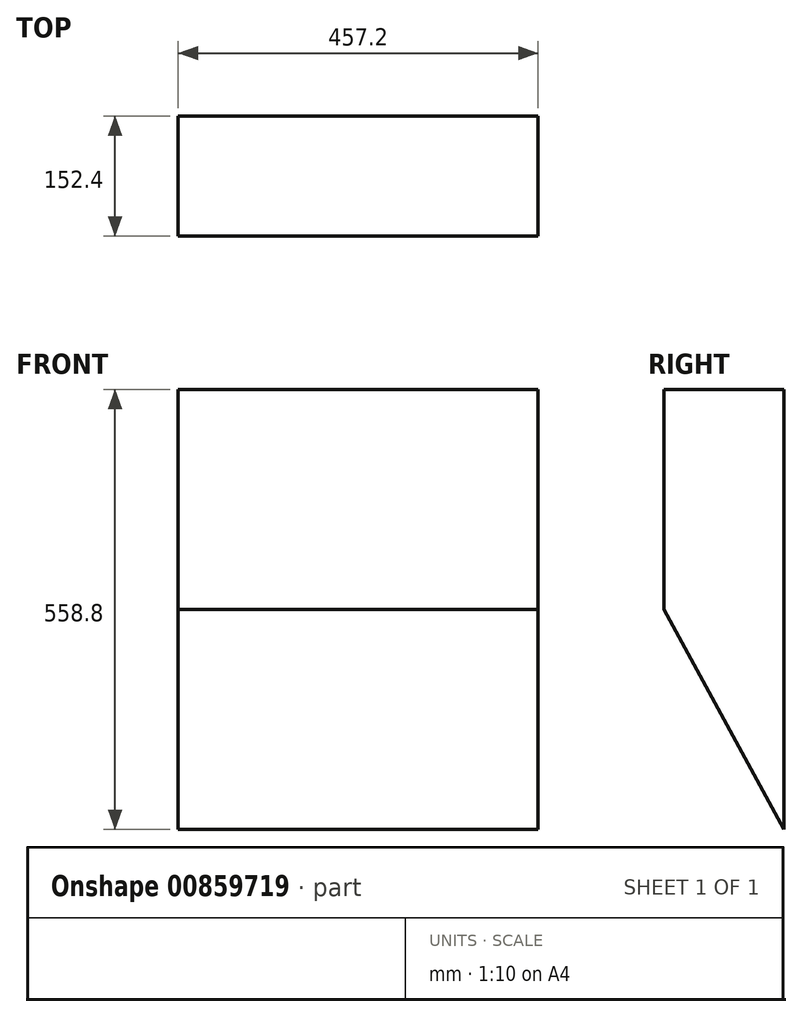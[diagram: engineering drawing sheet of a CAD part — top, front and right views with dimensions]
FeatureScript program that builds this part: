
annotation { "Feature Type Name" : "Feature", "Feature Type Description" : "" }
export const myFeature = defineFeature(function(context is Context, id is Id, definition is map)
    precondition{}
    {
        {
            var Q0;
            Q0=qCreatedBy(makeId("Right.planeOp"),FACE);
            var sketch = newSketch(context, id + "F0", { "sketchPlane" : qUnion([Q0])});
            skLineSegment(sketch, "E0.bottom", {"start": v(31.31, 467.97) * mm, "end": v(-121.09, 467.97) * mm, "construction": true});
            skLineSegment(sketch, "E0.top", {"start": v(31.31, -90.83) * mm, "end": v(-121.09, -90.83) * mm, "construction": true});
            skLineSegment(sketch, "E0.left", {"start": v(31.31, 467.97) * mm, "end": v(31.31, -90.83) * mm, "construction": true});
            skLineSegment(sketch, "E0.right", {"start": v(-121.09, 467.97) * mm, "end": v(-121.09, -90.83) * mm, "construction": true});
            skLineSegment(sketch, "E1", {"start": v(31.31, 467.97) * mm, "end": v(-121.09, 467.97) * mm});
            skLineSegment(sketch, "E2", {"start": v(-121.09, 188.57) * mm, "end": v(31.31, -90.83) * mm});
            skLineSegment(sketch, "E3", {"start": v(31.31, 467.97) * mm, "end": v(31.31, -90.83) * mm});
            skLineSegment(sketch, "E4", {"start": v(-121.09, 188.57) * mm, "end": v(-121.09, 467.97) * mm});
            skSolve(sketch);
        }
        {
            var Q0;
            Q0=makeQuery(id+"F0.imprint","IMPRINT",FACE,{"disambiguationData":[TD([[makeQuery(id+"F0.imprint","IMPRINT",EDGE,{"derivedFrom":sQuery(id+"F0.wireOp",EDGE,"E1")}),1.0]])]});
            extrude(context, id + "F1", {"entities" : qUnion([Q0]), "depth" : 457.2 * mm, "offsetDistance" : 25.4 * mm});
        }
    });
